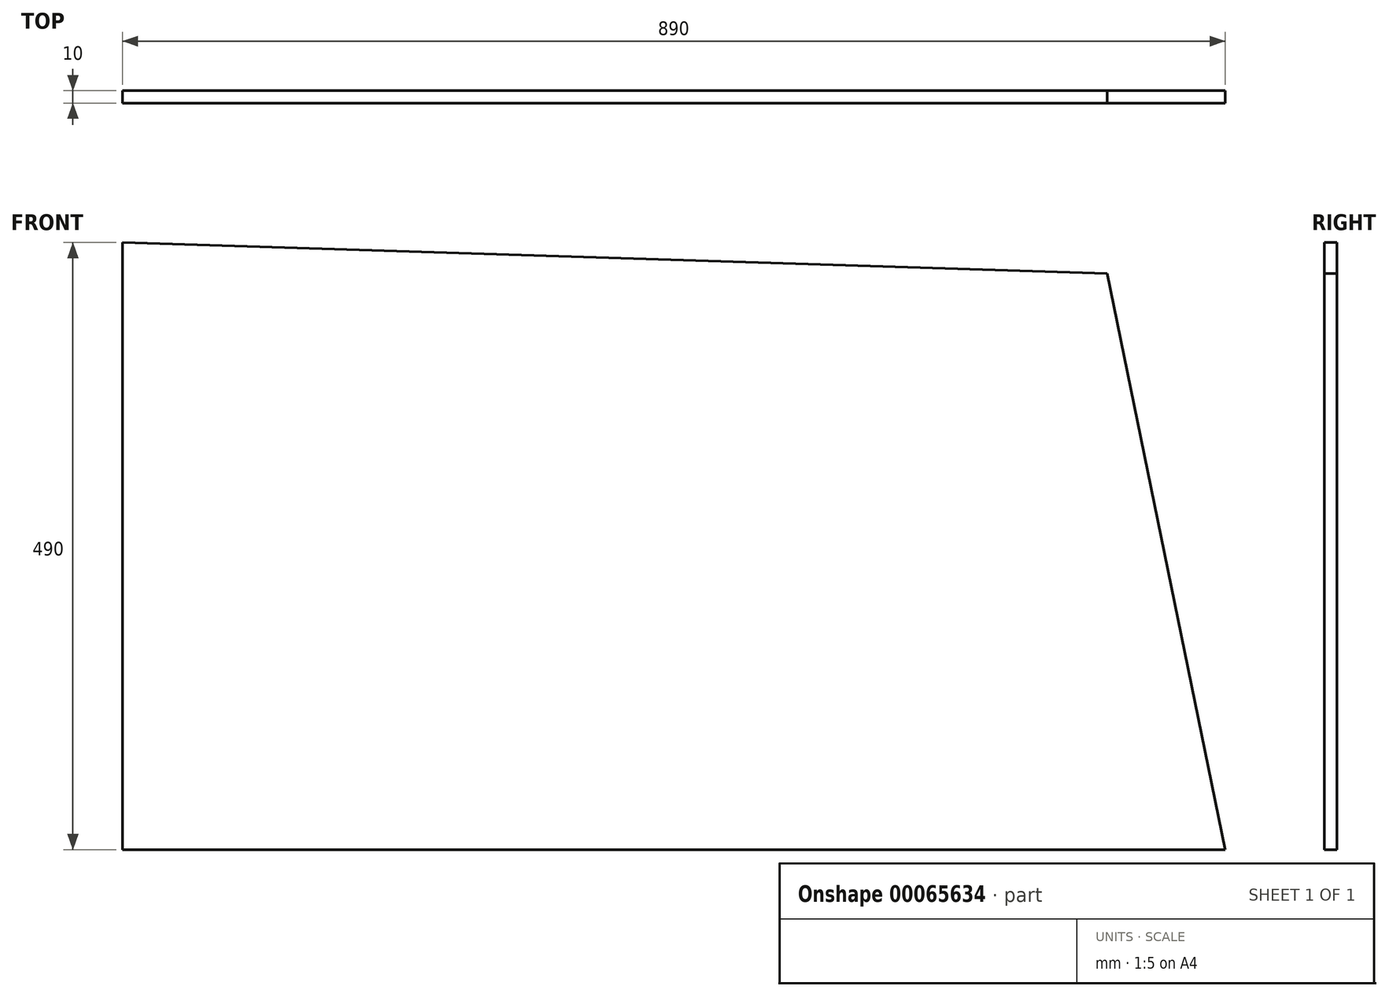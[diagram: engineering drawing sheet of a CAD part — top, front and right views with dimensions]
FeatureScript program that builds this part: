
annotation { "Feature Type Name" : "Feature", "Feature Type Description" : "" }
export const myFeature = defineFeature(function(context is Context, id is Id, definition is map)
    precondition{}
    {
        {
            var Q0;
            Q0=qCreatedBy(makeId("Front.planeOp"),FACE);
            var sketch = newSketch(context, id + "F0", { "sketchPlane" : qUnion([Q0])});
            skLineSegment(sketch, "E0.bottom", {"start": v(0, 0) * mm, "end": v(890, 0) * mm});
            skLineSegment(sketch, "E0.top", {"start": v(0, 490) * mm, "end": v(794.6, 465) * mm});
            skLineSegment(sketch, "E0.left", {"start": v(0, 0) * mm, "end": v(0, 490) * mm});
            skLineSegment(sketch, "E0.right", {"start": v(890, 0) * mm, "end": v(794.6, 465) * mm});
            skLineSegment(sketch, "E1", {"start": v(794.6, 465) * mm, "end": v(794.6, 0) * mm, "construction": true});
            skSolve(sketch);
        }
        {
            var Q0;
            Q0 = qSketchRegion(id + "F0", true);
            extrude(context, id + "F1", {"entities" : qUnion([Q0]), "depth" : 10 * mm});
        }
    });
